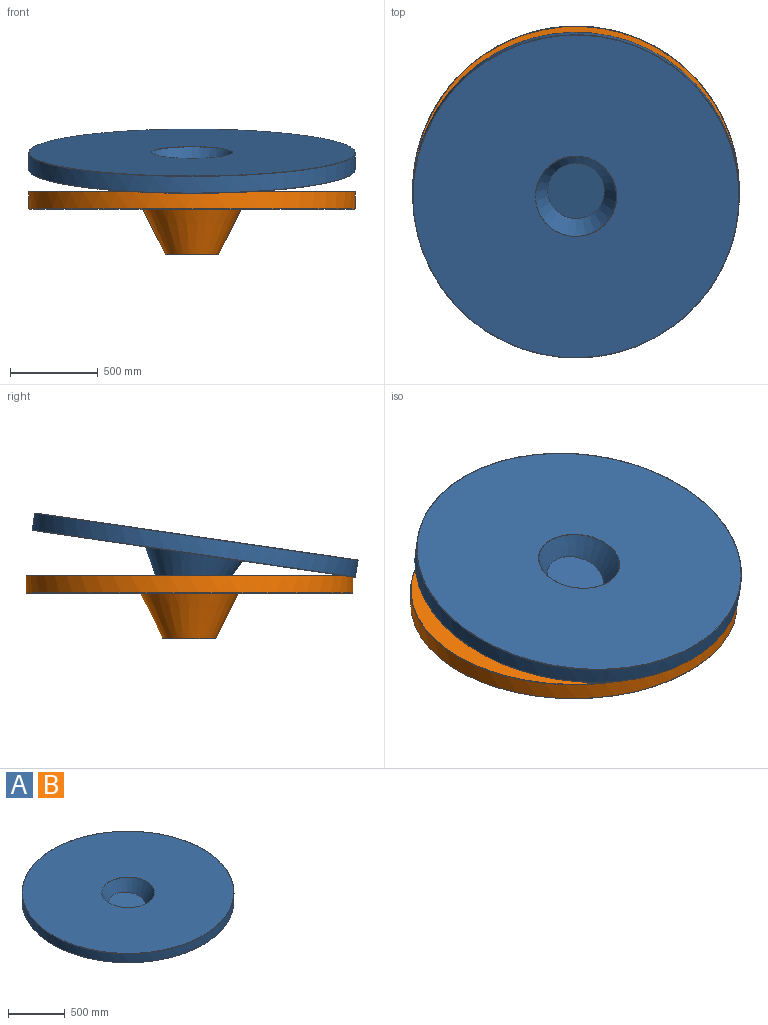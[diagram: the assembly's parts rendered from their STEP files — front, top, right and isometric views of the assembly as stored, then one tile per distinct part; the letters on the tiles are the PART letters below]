
ASSEMBLY  parts=2 mates=1
PART A: 15 faces, bbox 2015.2x2015.2x361.8 mm
  f0: cone r=230.91mm half-angle=26.6deg, axis (0,0,1), area 186745.7mm2, adj f6,f11
  f1: plane 297.53x297.53mm, normal (0,0,-1), area 69525.7mm2, adj f10
  f2: plane 1857.83x1857.83mm, normal (0,0,1), area 2541512.1mm2, adj f6,f7
  f3: cylinder r=930.91mm len=1861.83mm, axis (0,0,1), area 561514.5mm2, adj f7,f8
  f4: plane 1857.83x1857.83mm, normal (0,0,-1), area 2460725.8mm2, adj f8,f9
  f5: cone r=150mm half-angle=26.6deg, axis (0,0,1), area 392944.4mm2, adj f9,f10
  f6: torus R=232.15mm, axis (0,0,-1), area 3216mm2, adj f0,f2
  f7: torus R=928.91mm, axis (0,0,-1), area 18361.2mm2, adj f2,f3
  f8: torus R=928.91mm, axis (0,0,1), area 18361.2mm2, adj f3,f4
  f9: torus R=282.15mm, axis (0,0,1), area 3911.6mm2, adj f4,f5
  f10: torus R=148.76mm, axis (0,0,1), area 2083.6mm2, adj f1,f5
  f11: plane 325.9x325.04mm, normal (0,-0.14,0.99), area 84076.6mm2, adj f0
  f12: torus R=148.76mm, axis (0,0,-1), area 183.7mm2, adj f13,f14
  f13: plane 106.58x9.87mm, normal (0,0,1), area 706.2mm2, adj f12,f14
  f14: plane 107.1x11.62mm, normal (0,-0.09,-1), area 870.9mm2, adj f12,f13
PART B: same geometry as A
PLACE A rot(axis=(1,0,0),8.3deg) t=(0,-523.72,434.41)mm
PLACE B t=(0,-535.59,208.5)mm
MATE fastened A.f0 <-> B.f11  axis (0,0.14,-0.99) through (0,-523.72,434.41)mm
